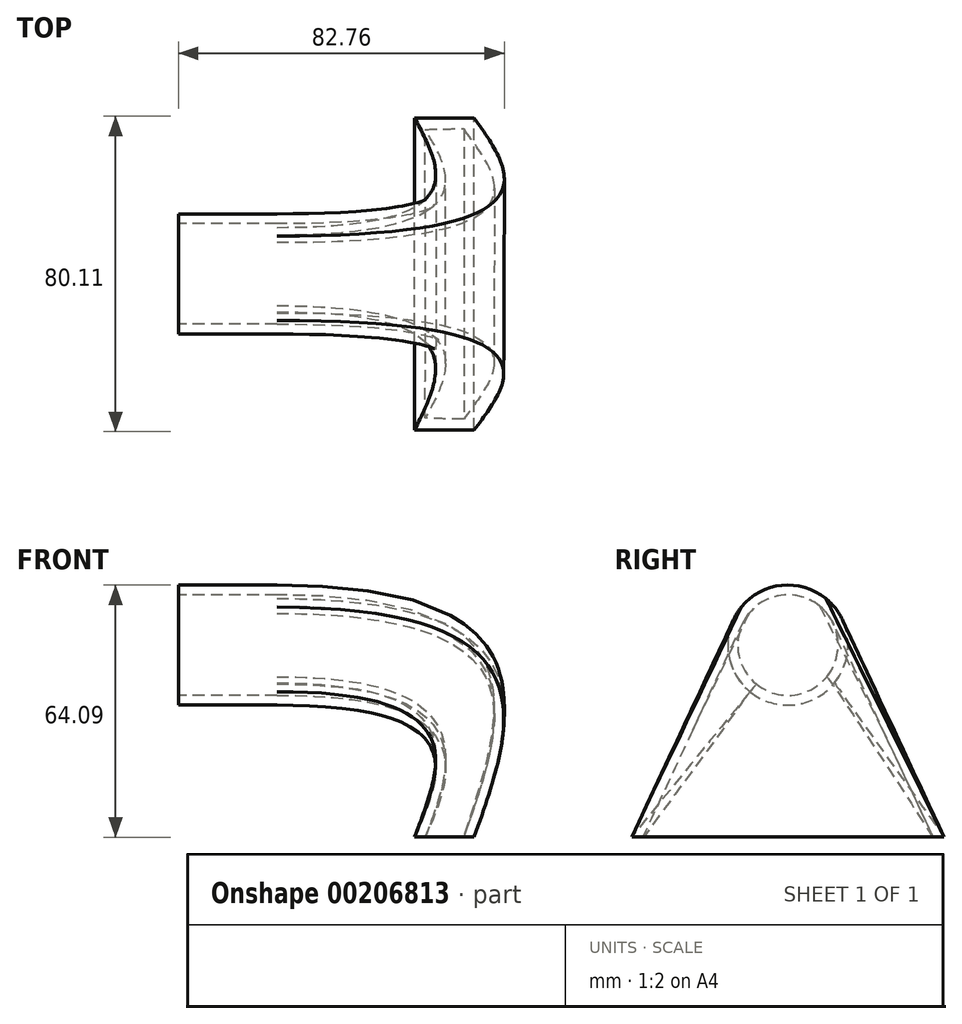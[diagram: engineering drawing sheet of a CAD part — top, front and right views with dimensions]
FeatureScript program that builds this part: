
annotation { "Feature Type Name" : "Feature", "Feature Type Description" : "" }
export const myFeature = defineFeature(function(context is Context, id is Id, definition is map)
    precondition{}
    {
        {
            var Q0;
            Q0=qCreatedBy(makeId("Top.planeOp"),FACE);
            var sketch = newSketch(context, id + "F0", { "sketchPlane" : qUnion([Q0])});
            skLineSegment(sketch, "E0.bottom", {"start": v(50.1, -39.63) * mm, "end": v(34.96, -39.63) * mm});
            skLineSegment(sketch, "E0.top", {"start": v(50.1, 39.63) * mm, "end": v(34.96, 39.63) * mm});
            skLineSegment(sketch, "E0.left", {"start": v(50.1, -39.63) * mm, "end": v(50.1, 39.63) * mm});
            skLineSegment(sketch, "E0.right", {"start": v(34.96, -39.63) * mm, "end": v(34.96, 39.63) * mm});
            skPoint(sketch, "E0.middle", {"position": v(42.53, 0) * mm});
            skSolve(sketch);
        }
        {
            var Q0;
            Q0=qCreatedBy(makeId("Right.planeOp"),FACE);
            var sketch = newSketch(context, id + "F1", { "sketchPlane" : qUnion([Q0])});
            skCircle(sketch, "E1", {"center": v(0, 48.71) * mm, "radius": 15.26 * mm});
            skSolve(sketch);
        }
        {
            var Q0;
            Q0=makeQuery(id+"F1.imprint","IMPRINT",FACE,{"disambiguationData":[TD([[makeQuery(id+"F1.imprint","IMPRINT",EDGE,{"derivedFrom":sQuery(id+"F1.wireOp",EDGE,"E1")}),1.0]])]});
            var Q1;
            Q1=makeQuery(id+"F0.imprint","IMPRINT",FACE,{"disambiguationData":[TD([[makeQuery(id+"F0.imprint","IMPRINT",EDGE,{"derivedFrom":sQuery(id+"F0.wireOp",EDGE,"E0.bottom")}),-1.0]])]});
            loft(context, id + "F2", {"startCondition" : LoftEndDerivativeType.NORMAL_TO_PROFILE, "startMagnitude" : 4, "sheetProfilesArray" : [{ "sheetProfileEntities" : qUnion([Q0]) }, { "sheetProfileEntities" : qUnion([Q1]) }]});
        }
        {
            var Q0;
            Q0=makeQuery(id+"F2.opLoft","CAP_FACE",FACE,{"disambiguationData":[OSD([makeQuery(id+"F1.imprint","IMPRINT",FACE,{"disambiguationData":[TD([[makeQuery(id+"F1.imprint","IMPRINT",EDGE,{"derivedFrom":sQuery(id+"F1.wireOp",EDGE,"E1")}),1.0]])]})])],"isStart":true});
            extrude(context, id + "F3", {"entities" : qUnion([Q0]), "operationType" : NewBodyOperationType.ADD, "depth" : 25 * mm});
        }
        {
            var Q0;
            Q0=makeQuery(id+"F3.opExtrude","CAP_FACE",FACE,{"disambiguationData":[OSD([makeQuery(id+"F1.imprint","IMPRINT",FACE,{"disambiguationData":[TD([[makeQuery(id+"F1.imprint","IMPRINT",EDGE,{"derivedFrom":sQuery(id+"F1.wireOp",EDGE,"E1")}),1.0]])]})])],"isStart":false});
            var Q1;
            Q1=makeQuery(id+"F2.opLoft","CAP_FACE",FACE,{"disambiguationData":[OSD([makeQuery(id+"F0.imprint","IMPRINT",FACE,{"disambiguationData":[TD([[makeQuery(id+"F0.imprint","IMPRINT",EDGE,{"derivedFrom":sQuery(id+"F0.wireOp",EDGE,"E0.bottom")}),-1.0]])]})])],"isStart":true});
            shell(context, id + "F4", {"entities" : qUnion([Q0, Q1]), "thickness" : 2.5 * mm});
        }
    });
